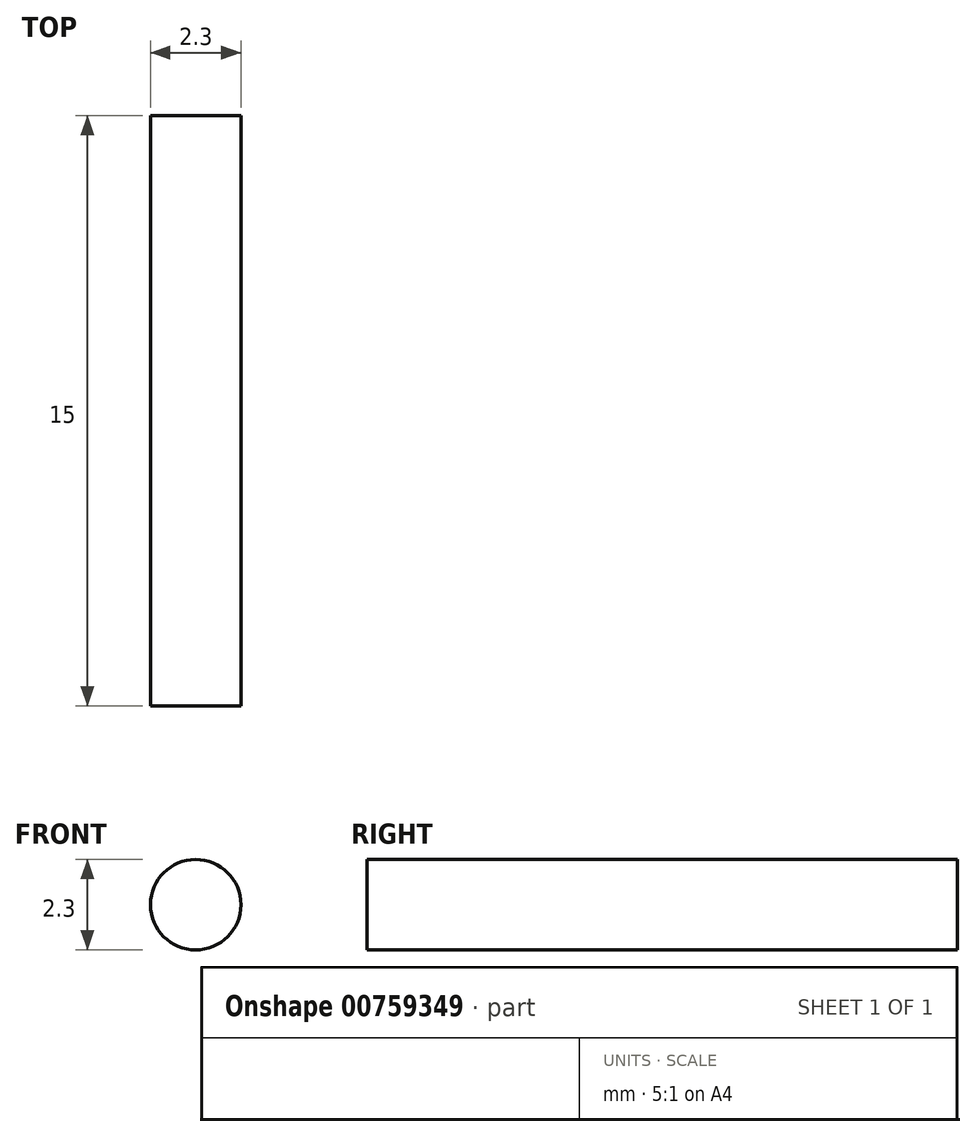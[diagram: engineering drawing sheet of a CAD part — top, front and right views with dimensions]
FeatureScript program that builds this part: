
annotation { "Feature Type Name" : "Feature", "Feature Type Description" : "" }
export const myFeature = defineFeature(function(context is Context, id is Id, definition is map)
    precondition{}
    {
        {
            var Q0;
            Q0=qCreatedBy(makeId("Front.planeOp"),FACE);
            var sketch = newSketch(context, id + "F0", { "sketchPlane" : qUnion([Q0])});
            skCircle(sketch, "E0", {"center": v(0, 0) * mm, "radius": 1.15 * mm});
            skSolve(sketch);
        }
        {
            var Q0;
            Q0=makeQuery(id+"F0.imprint","IMPRINT",FACE,{"disambiguationData":[TD([[makeQuery(id+"F0.imprint","IMPRINT",EDGE,{"derivedFrom":sQuery(id+"F0.wireOp",EDGE,"E0")}),1.0]])]});
            extrude(context, id + "F1", {"entities" : qUnion([Q0]), "depth" : 15 * mm, "offsetDistance" : 25 * mm});
        }
    });
